# Revit family: Deca_Tanque_TQ.03_40 LitrosGGGGGGGGG
name_source: partatom
category: Plumbing Fixtures
revit_build: Autodesk Revit Architecture 2012 (Build: 20120126_0600(x64)
units: mm (PartAtom-declared; Revit-internal decimal feet)

## types (1)
- TQ.03_Branco Gelo GE17
    Aprovado por = Contino/quattroD
    Assembly Code = D2010400
    Atendimento ao Cliente = 0800-0117073
    Coluna = Deca GE17 Branco Gelo Cerâmica
    Coluna-Family = Deca_Shared_Coluna para Tanque_TQ.03 : CT.25_Branco Gelo GE17
    Criado por = Contino/quattroD
    Cuba = Deca GE17 Branco Gelo Cerâmica
    Código = TQ.03.17
    Default Elevation = 0 mm  [stored 0 ft]
    Description = Tanque
    Diâmetro Ponto de Esgoto = 40 mm  [stored 0.131234 ft]
    Flow Pressure = 0.00 psi
    Informações Complementares = Capacidade total: 40 litros. Obrigatório o uso da coluna
    Linha = Tanque
    Louça/Metais = Louça
    Manufacturer = Deca
    Material = Deca_Vitreous China
    Model = TQ.03.17
    Norma = ABNT NBR 15097-1: 2011 / ABNT NBR 15097-2: 2011
    Peso Liquido (Kg) = 24.8
    Produto = Tanque - 40 litros
    Raio Ponto de Esgoto = 20 mm  [stored 0.0656168 ft]
    Segmento = Médio
    URL = www.deca.com.br/produtos
    Variações de COR = Branco (TQ.03.17).
    Vendido Separadamente = Válvula de escoamento tanque sem ladrão 1 1/2 DN40: Cromado (1606.C.112); Parafusos para fixação tanque: Cromado (FT.11.01); Sifão para tanque 1680.C.114 ou 1680.C.112
    WFU = 0

note: [stored X ft] marks values corroborated as IEEE doubles in the binary element streams (Revit-internal decimal feet)

## geometry (parser evidence)
native form markers: Blend x2, Sweep x5
no freeform markers — native parametric forms only
